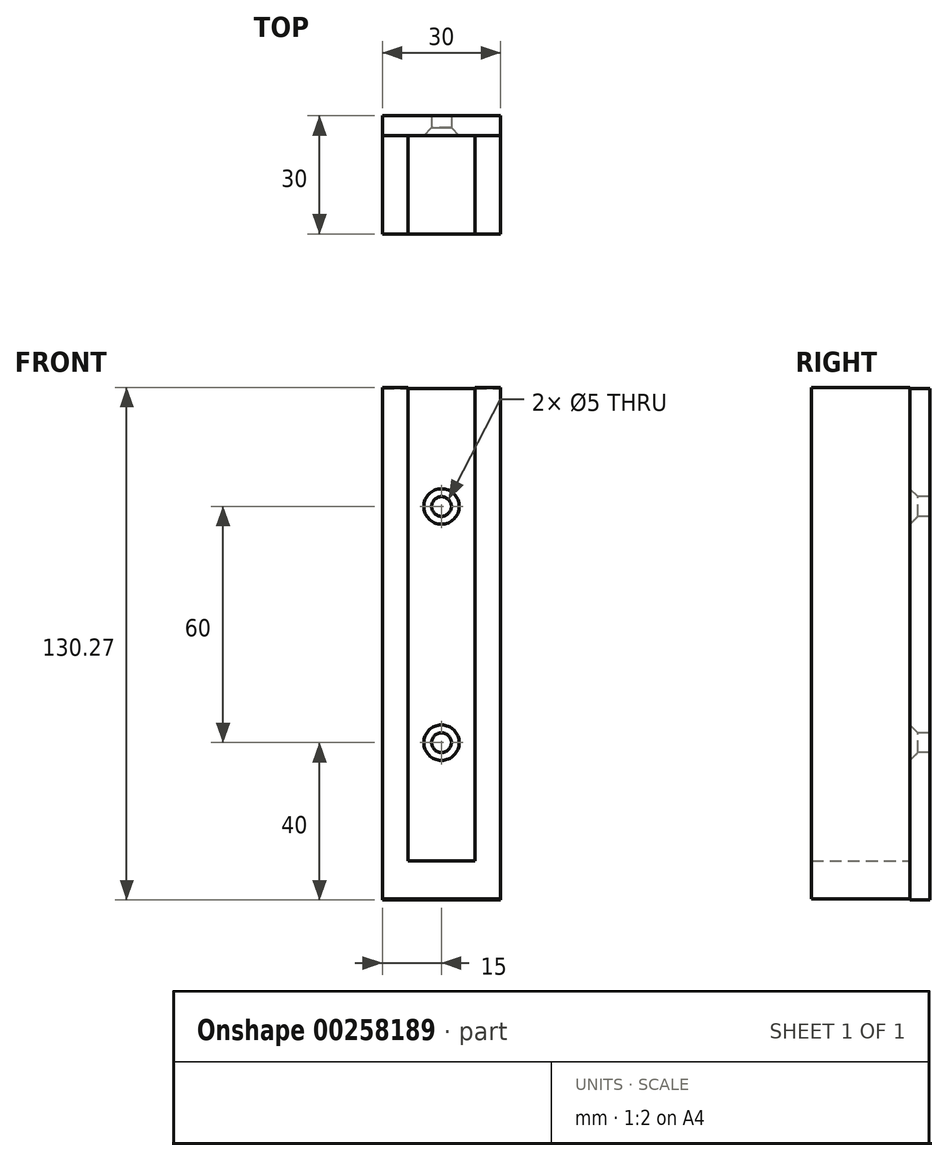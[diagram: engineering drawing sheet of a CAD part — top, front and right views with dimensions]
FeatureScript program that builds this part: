
annotation { "Feature Type Name" : "Feature", "Feature Type Description" : "" }
export const myFeature = defineFeature(function(context is Context, id is Id, definition is map)
    precondition{}
    {
        {
            var Q0;
            Q0=qCreatedBy(makeId("Front.planeOp"),FACE);
            var sketch = newSketch(context, id + "F0", { "sketchPlane" : qUnion([Q0])});
            skLineSegment(sketch, "E0", {"start": v(0, 60.27) * mm, "end": v(0, -69.73) * mm, "construction": true});
            skLineSegment(sketch, "E1", {"start": v(-65.07, 0) * mm, "end": v(56.56, 0) * mm, "construction": true});
            skLineSegment(sketch, "E2.0", {"start": v(-8.5, 60.27) * mm, "end": v(-8.5, -60) * mm});
            skLineSegment(sketch, "E3.0", {"start": v(8.5, 60.27) * mm, "end": v(8.5, -60) * mm});
            skLineSegment(sketch, "E4.0", {"start": v(-15, 60.27) * mm, "end": v(-15, -69.73) * mm});
            skLineSegment(sketch, "E5.0", {"start": v(15, 60.27) * mm, "end": v(15, -69.73) * mm});
            skLineSegment(sketch, "E6", {"start": v(-15, 60.27) * mm, "end": v(-8.5, 60.27) * mm});
            skLineSegment(sketch, "E7", {"start": v(8.5, 60.27) * mm, "end": v(15, 60.27) * mm});
            skLineSegment(sketch, "E8", {"start": v(15, -69.73) * mm, "end": v(-15, -69.73) * mm});
            skLineSegment(sketch, "E9.0", {"start": v(-8.5, -60) * mm, "end": v(8.5, -60) * mm});
            skSolve(sketch);
        }
        {
            var Q0;
            Q0=makeQuery(id+"F0.imprint","IMPRINT",FACE,{"disambiguationData":[TD([[makeQuery(id+"F0.imprint","IMPRINT",EDGE,{"derivedFrom":sQuery(id+"F0.wireOp",EDGE,"E2.0")}),-1.0]])]});
            extrude(context, id + "F1", {"entities" : qUnion([Q0]), "depth" : 25 * mm});
        }
        {
            var Q0;
            Q0=qCreatedBy(makeId("Front.planeOp"),FACE);
            var sketch = newSketch(context, id + "F2", { "sketchPlane" : qUnion([Q0])});
            skLineSegment(sketch, "E10.0", {"start": v(15, 0) * mm, "end": v(15, 60) * mm});
            skLineSegment(sketch, "E11.0", {"start": v(15, 0) * mm, "end": v(15, -70) * mm});
            skLineSegment(sketch, "E12.0", {"start": v(-15, 0) * mm, "end": v(-15, -70) * mm});
            skLineSegment(sketch, "E13.0", {"start": v(-15, 0) * mm, "end": v(-15, 60) * mm});
            skLineSegment(sketch, "E14.0", {"start": v(-15, -70) * mm, "end": v(15, -70) * mm});
            skLineSegment(sketch, "E15.0", {"start": v(-15, 60) * mm, "end": v(15, 60) * mm});
            skPoint(sketch, "E16.orphan", {"position": v(-28.85, 0) * mm});
            skLineSegment(sketch, "E17.0", {"start": v(-15, 30) * mm, "end": v(15, 30) * mm, "construction": true});
            skLineSegment(sketch, "E18", {"start": v(0, 43.06) * mm, "end": v(0, 15.58) * mm, "construction": true});
            skPoint(sketch, "E18.endSnap0", {"position": v(0, 30) * mm});
            skLineSegment(sketch, "E19.0", {"start": v(-28.85, -30) * mm, "end": v(34.84, -30) * mm, "construction": true});
            skLineSegment(sketch, "E20", {"start": v(0, 0) * mm, "end": v(0, -50.7) * mm, "construction": true});
            skCircle(sketch, "E21", {"center": v(0, -30) * mm, "radius": 1.24 * mm});
            skSolve(sketch);
        }
        {
            var Q0;
            Q0=makeQuery(id+"F2.imprint","IMPRINT",FACE,{"disambiguationData":[TD([[makeQuery(id+"F2.imprint","IMPRINT",EDGE,{"derivedFrom":sQuery(id+"F2.wireOp",EDGE,"E10.0")}),1.0]])]});
            extrude(context, id + "F3", {"entities" : qUnion([Q0]), "oppositeDirection" : true, "depth" : 5 * mm});
        }
        {
            var Q0;
            Q0=sQuery(id+"F2.wireOp",VERTEX,"E18.endSnap0");
            var Q1;
            Q1=sQuery(id+"F2.wireOp",VERTEX,"E21.center");
            var Q2;
            Q2=makeQuery(id+"F3.opExtrude","SWEPT_BODY",BODY,{"disambiguationData":[OSD([sQuery(id+"F2.wireOp",EDGE,"E10.0"),sQuery(id+"F2.wireOp",EDGE,"E11.0"),sQuery(id+"F2.wireOp",EDGE,"E12.0"),sQuery(id+"F2.wireOp",EDGE,"E13.0"),sQuery(id+"F2.wireOp",EDGE,"E14.0"),sQuery(id+"F2.wireOp",EDGE,"E15.0")])]});
            hole(context, id + "F4", {"style" : HoleStyle.C_SINK, "endStyle" : HoleEndStyle.THROUGH, "holeDiameter" : 5 * mm, "cSinkDiameter" : 9 * mm, "cSinkAngle" : 90 * degree, "tappedDepth" : 12 * mm, "tapClearance" : 3, "startFromSketch" : true, "locations" : qUnion([Q0, Q1]), "scope" : qUnion([Q2])});
        }
    });
